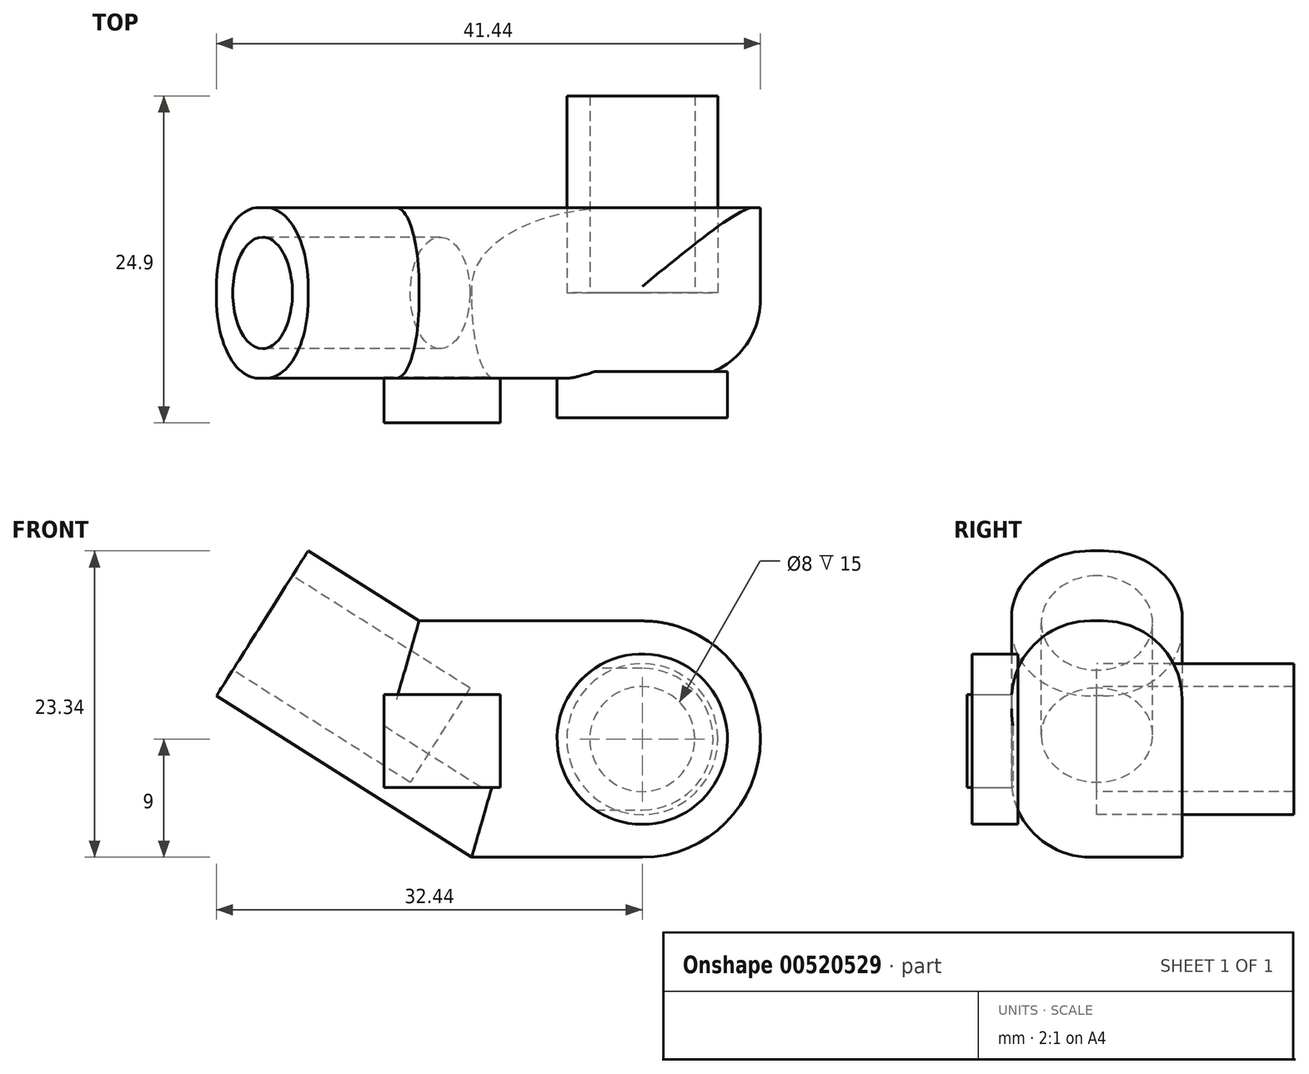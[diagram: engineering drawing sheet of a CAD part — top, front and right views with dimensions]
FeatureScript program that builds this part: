
annotation { "Feature Type Name" : "Feature", "Feature Type Description" : "" }
export const myFeature = defineFeature(function(context is Context, id is Id, definition is map)
    precondition{}
    {
        {
            var Q0;
            Q0=qCreatedBy(makeId("Front.planeOp"),FACE);
            var sketch = newSketch(context, id + "F0", { "sketchPlane" : qUnion([Q0])});
            skCircle(sketch, "E0", {"center": v(0, 0) * mm, "radius": 9 * mm});
            skLineSegment(sketch, "E1", {"start": v(0, -9) * mm, "end": v(-13, -9) * mm});
            skLineSegment(sketch, "E2", {"start": v(-13, -9) * mm, "end": v(-32.44, 3.3) * mm});
            skLineSegment(sketch, "E3", {"start": v(-32.44, 3.3) * mm, "end": v(-25.45, 14.34) * mm});
            skLineSegment(sketch, "E4", {"start": v(-25.45, 14.34) * mm, "end": v(-17, 9) * mm});
            skLineSegment(sketch, "E5", {"start": v(-17, 9) * mm, "end": v(0, 9) * mm});
            skSolve(sketch);
        }
        {
            var Q0;
            {var subQ0=sQuery(id+"F0.wireOp",EDGE,"E1");Q0=makeQuery(id+"F0.imprint","IMPRINT",FACE,{"disambiguationData":[TD([[makeQuery(id+"F0.imprint","IMPRINT",EDGE,{"derivedFrom":subQ0}),-1.0]])]});}
            var Q1;
            {var subQ0=sQuery(id+"F0.wireOp",EDGE,"E0");var subQ1=makeQuery(id+"F0.imprint","INTERSECT",VERTEX,{"derivedFrom":[subQ0,sQuery(id+"F0.wireOp",EDGE,"E1")]});Q1=makeQuery(id+"F0.imprint","IMPRINT",FACE,{"disambiguationData":[TD([[makeQuery(id+"F0.imprint","IMPRINT",EDGE,{"disambiguationData":[TD([[subQ1,1.0]])],"derivedFrom":subQ0}),1.0]])]});}
            extrude(context, id + "F1", {"entities" : qUnion([Q0, Q1]), "endBound" : BoundingType.SYMMETRIC, "depth" : 13 * mm});
        }
        {
            var Q0;
            Q0=makeQuery(id+"F1.opExtrude","SWEPT_FACE",FACE,{"disambiguationData":[OSD([sQuery(id+"F0.wireOp",EDGE,"E3")])]});
            var sketch = newSketch(context, id + "F2", { "sketchPlane" : qUnion([Q0])});
            skCircle(sketch, "E6", {"center": v(0, -7.98) * mm, "radius": 4.25 * mm});
            skSolve(sketch);
        }
        {
            var Q0;
            Q0=qSketchRegion(id+"F2",true);
            extrude(context, id + "F3", {"entities" : qUnion([Q0]), "operationType" : NewBodyOperationType.REMOVE, "oppositeDirection" : true, "depth" : 16 * mm});
        }
        {
            var Q0;
            Q0=makeQuery(id+"F1.opExtrude","CAP_EDGE",EDGE,{"disambiguationData":[OSD([sQuery(id+"F0.wireOp",EDGE,"E4")])],"isStart":true});
            var Q1;
            Q1=makeQuery(id+"F1.opExtrude","CAP_EDGE",EDGE,{"disambiguationData":[OSD([sQuery(id+"F0.wireOp",EDGE,"E5")])],"isStart":true});
            var Q2;
            Q2=makeQuery(id+"F1.opExtrude","CAP_EDGE",EDGE,{"disambiguationData":[OSD([sQuery(id+"F0.wireOp",EDGE,"E2")])],"isStart":true});
            fillet(context, id + "F4", {"entities" : qUnion([Q0, Q1, Q2]), "radius" : 6 * mm, "tangentPropagation" : true, "allowEdgeOverflow" : false});
        }
        {
            var Q0;
            Q0=makeQuery(id+"F1.opExtrude","CAP_EDGE",EDGE,{"disambiguationData":[OSD([sQuery(id+"F0.wireOp",EDGE,"E4")])],"isStart":false});
            var Q1;
            Q1=makeQuery(id+"F1.opExtrude","CAP_EDGE",EDGE,{"disambiguationData":[OSD([sQuery(id+"F0.wireOp",EDGE,"E5")])],"isStart":false});
            var Q2;
            Q2=makeQuery(id+"F1.opExtrude","CAP_EDGE",EDGE,{"disambiguationData":[OSD([sQuery(id+"F0.wireOp",EDGE,"E2")])],"isStart":false});
            fillet(context, id + "F5", {"entities" : qUnion([Q0, Q1, Q2]), "radius" : 6 * mm, "allowEdgeOverflow" : false});
        }
        {
            var Q0;
            Q0=qCreatedBy(makeId("Front.planeOp"),FACE);
            var sketch = newSketch(context, id + "F6", { "sketchPlane" : qUnion([Q0])});
            skCircle(sketch, "E7", {"center": v(0, 0) * mm, "radius": 4 * mm});
            skCircle(sketch, "E8", {"center": v(0, 0) * mm, "radius": 5.75 * mm});
            skSolve(sketch);
        }
        {
            var Q0;
            Q0=makeQuery(id+"F6.imprint","IMPRINT",FACE,{"disambiguationData":[TD([[makeQuery(id+"F6.imprint","IMPRINT",EDGE,{"derivedFrom":sQuery(id+"F6.wireOp",EDGE,"E7")}),-1.0]])]});
            var Q1;
            Q1=sQuery(id+"F6.wireOp",EDGE,"E7");
            var Q2;
            Q2=sQuery(id+"F6.wireOp",EDGE,"E8");
            extrude(context, id + "F7", {"entities" : qUnion([Q0]), "surfaceEntities" : qUnion([Q1, Q2]), "depth" : 15 * mm});
        }
        {
            var Q0;
            Q0=makeQuery(id+"F1.opExtrude","SWEPT_BODY",BODY,{"disambiguationData":[OSD([sQuery(id+"F0.wireOp",EDGE,"E0"),sQuery(id+"F0.wireOp",EDGE,"E1"),sQuery(id+"F0.wireOp",EDGE,"E2"),sQuery(id+"F0.wireOp",EDGE,"E3"),sQuery(id+"F0.wireOp",EDGE,"E4"),sQuery(id+"F0.wireOp",EDGE,"E5")])]});
            var Q1;
            Q1=makeQuery(id+"F7.opExtrude","SWEPT_BODY",BODY,{"disambiguationData":[OSD([sQuery(id+"F6.wireOp",EDGE,"E7"),sQuery(id+"F6.wireOp",EDGE,"E8")])]});
            var Q2;
            Q2=makeQuery(id+"F7.opExtrude","SWEPT_FACE",FACE,{"disambiguationData":[OSD([sQuery(id+"F6.wireOp",EDGE,"E8")])]});
            var Q3;
            Q3=qCreatedBy(makeId("Front.planeOp"),FACE);
            mirror(context, id + "F8", {"entities" : qUnion([Q0, Q1]), "faces" : qUnion([Q2]), "mirrorPlane" : qUnion([Q3])});
        }
        {
            var Q0;
            Q0=makeQuery(id+"F7.opExtrude","SWEPT_BODY",BODY,{"disambiguationData":[OSD([sQuery(id+"F6.wireOp",EDGE,"E7"),sQuery(id+"F6.wireOp",EDGE,"E8")])]});
            deleteBodies(context, id + "F9", {"entities" : qUnion([Q0])});
        }
        {
            var Q0;
            Q0=makeQuery(id+"F1.opExtrude","SWEPT_BODY",BODY,{"disambiguationData":[OSD([sQuery(id+"F0.wireOp",EDGE,"E0"),sQuery(id+"F0.wireOp",EDGE,"E1"),sQuery(id+"F0.wireOp",EDGE,"E2"),sQuery(id+"F0.wireOp",EDGE,"E3"),sQuery(id+"F0.wireOp",EDGE,"E4"),sQuery(id+"F0.wireOp",EDGE,"E5")])]});
            deleteBodies(context, id + "F10", {"entities" : qUnion([Q0])});
        }
        {
            var Q0;
            Q0=qCreatedBy(makeId("Front.planeOp"),FACE);
            var sketch = newSketch(context, id + "F11", { "sketchPlane" : qUnion([Q0])});
            skCircle(sketch, "E9", {"center": v(0, 0) * mm, "radius": 6.49 * mm});
            skSolve(sketch);
        }
        {
            var Q0;
            Q0 = qSketchRegion(id + "F11", true);
            extrude(context, id + "F12", {"entities" : qUnion([Q0]), "operationType" : NewBodyOperationType.ADD, "depth" : 9.5 * mm, "offsetDistance" : 25 * mm, "hasSecondDirection" : true, "secondDirectionOppositeDirection" : false, "secondDirectionDepth" : 6 * mm});
        }
        {
            var Q0;
            Q0=qCreatedBy(makeId("Front.planeOp"),FACE);
            var sketch = newSketch(context, id + "F13", { "sketchPlane" : qUnion([Q0])});
            skLineSegment(sketch, "E10.bottom", {"start": v(-10.8, 3.4) * mm, "end": v(-19.69, 3.4) * mm});
            skLineSegment(sketch, "E10.top", {"start": v(-10.8, -3.7) * mm, "end": v(-19.69, -3.7) * mm});
            skLineSegment(sketch, "E10.left", {"start": v(-10.8, 3.4) * mm, "end": v(-10.8, -3.7) * mm});
            skLineSegment(sketch, "E10.right", {"start": v(-19.69, 3.4) * mm, "end": v(-19.69, -3.7) * mm});
            skSolve(sketch);
        }
        {
            var Q0;
            Q0 = qSketchRegion(id + "F13", true);
            extrude(context, id + "F14", {"entities" : qUnion([Q0]), "operationType" : NewBodyOperationType.ADD, "depth" : 9.9 * mm, "offsetDistance" : 25 * mm, "hasSecondDirection" : true, "secondDirectionOppositeDirection" : false, "secondDirectionDepth" : 6.4 * mm});
        }
    });
